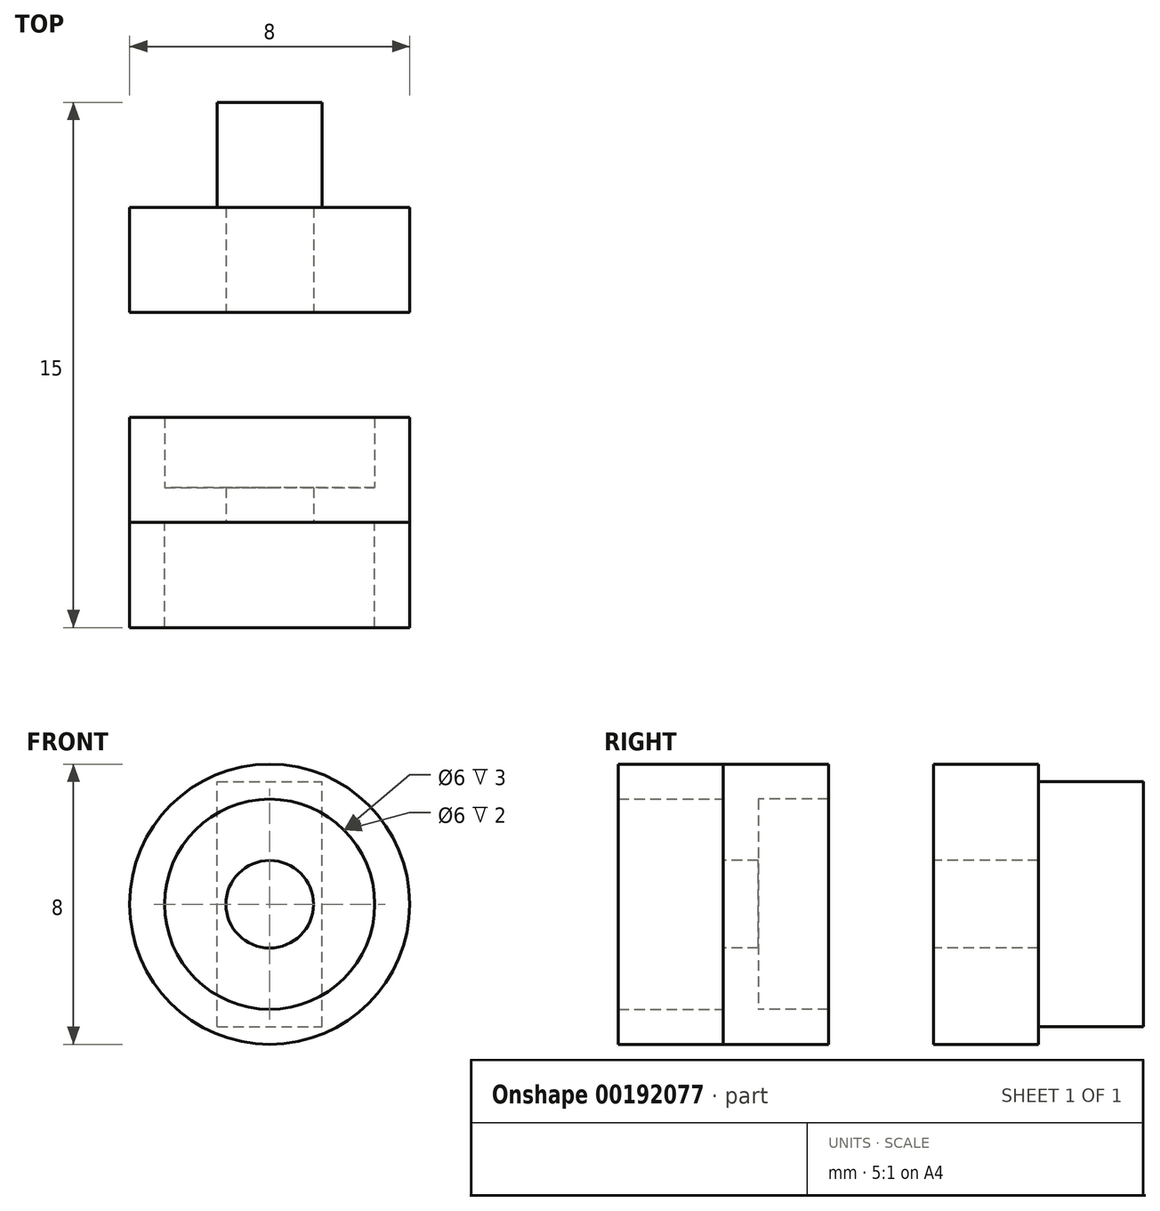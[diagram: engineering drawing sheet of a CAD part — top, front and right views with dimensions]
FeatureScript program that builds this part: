
annotation { "Feature Type Name" : "Feature", "Feature Type Description" : "" }
export const myFeature = defineFeature(function(context is Context, id is Id, definition is map)
    precondition{}
    {
        {
            var Q0;
            Q0=qCreatedBy(makeId("Front.planeOp"),FACE);
            var sketch = newSketch(context, id + "F0", { "sketchPlane" : qUnion([Q0])});
            skCircle(sketch, "E0", {"center": v(0, 0) * mm, "radius": 4 * mm});
            skSolve(sketch);
        }
        {
            var Q0;
            Q0 = qSketchRegion(id + "F0", true);
            extrude(context, id + "F1", {"entities" : qUnion([Q0]), "depth" : 1 * mm});
        }
        {
            var Q0;
            Q0=makeQuery(id+"F1.opExtrude","CAP_FACE",FACE,{"disambiguationData":[OSD([sQuery(id+"F0.wireOp",EDGE,"cq2fFx1E-zUqv-iU8P-xQMs-zw5kZQLWphNt"),sQuery(id+"F0.wireOp",EDGE,"E0")])],"isStart":true});
            var sketch = newSketch(context, id + "F2", { "sketchPlane" : qUnion([Q0])});
            skCircle(sketch, "E1", {"center": v(0, 0) * mm, "radius": 4 * mm});
            skCircle(sketch, "E2", {"center": v(0, 0) * mm, "radius": 3 * mm});
            skSolve(sketch);
        }
        {
            var Q0;
            Q0 = qSketchRegion(id + "F2", true);
            extrude(context, id + "F3", {"entities" : qUnion([Q0]), "operationType" : NewBodyOperationType.ADD, "depth" : 2 * mm});
        }
        {
            var Q0;
            Q0=makeQuery(id+"F1.opExtrude","CAP_FACE",FACE,{"disambiguationData":[OSD([sQuery(id+"F0.wireOp",EDGE,"E0")])],"isStart":false});
            var sketch = newSketch(context, id + "F4", { "sketchPlane" : qUnion([Q0])});
            skCircle(sketch, "E3", {"center": v(0, 0) * mm, "radius": 1.25 * mm});
            skSolve(sketch);
        }
        {
            var Q0;
            Q0 = qSketchRegion(id + "F4", true);
            extrude(context, id + "F5", {"entities" : qUnion([Q0]), "operationType" : NewBodyOperationType.REMOVE, "oppositeDirection" : true, "depth" : 25 * mm});
        }
        {
            var Q0;
            Q0=makeQuery(id+"F1.opExtrude","CAP_FACE",FACE,{"disambiguationData":[OSD([sQuery(id+"F0.wireOp",EDGE,"E0")])],"isStart":false});
            var sketch = newSketch(context, id + "F6", { "sketchPlane" : qUnion([Q0])});
            skCircle(sketch, "E4", {"center": v(0, 0) * mm, "radius": 4 * mm});
            skCircle(sketch, "E5", {"center": v(0, 0) * mm, "radius": 3 * mm});
            skSolve(sketch);
        }
        {
            var Q0;
            Q0 = qSketchRegion(id + "F6", true);
            extrude(context, id + "F7", {"entities" : qUnion([Q0]), "depth" : 3 * mm});
        }
        {
            var Q0;
            Q0=qCreatedBy(makeId("Front.planeOp"),FACE);
            cPlane(context, id + "F8", {"entities" : qUnion([Q0]), "cplaneType" : CPlaneType.OFFSET, "offset" : 5 * mm, "oppositeDirection" : true, "width" : 150 * mm, "height" : 150 * mm});
        }
        {
            var Q0;
            Q0=qCreatedBy(id+"F8.planeOp",FACE);
            var sketch = newSketch(context, id + "F9", { "sketchPlane" : qUnion([Q0])});
            skCircle(sketch, "E6", {"center": v(0, 0) * mm, "radius": 4 * mm});
            skSolve(sketch);
        }
        {
            var Q0;
            Q0 = qSketchRegion(id + "F9", true);
            extrude(context, id + "F10", {"entities" : qUnion([Q0]), "oppositeDirection" : true, "depth" : 3 * mm});
        }
        {
            var Q0;
            Q0=qCreatedBy(id+"F8.planeOp",FACE);
            cPlane(context, id + "F11", {"entities" : qUnion([Q0]), "cplaneType" : CPlaneType.OFFSET, "offset" : 4 * mm, "oppositeDirection" : true, "width" : 150 * mm, "height" : 150 * mm});
        }
        {
            var Q0;
            Q0=qCreatedBy(id+"F8.planeOp",FACE);
            var sketch = newSketch(context, id + "F12", { "sketchPlane" : qUnion([Q0])});
            skCircle(sketch, "E7", {"center": v(0, 0) * mm, "radius": 1.25 * mm});
            skSolve(sketch);
        }
        {
            var Q0;
            Q0 = qSketchRegion(id + "F12", true);
            extrude(context, id + "F13", {"entities" : qUnion([Q0]), "operationType" : NewBodyOperationType.REMOVE, "oppositeDirection" : true, "depth" : 3 * mm});
        }
        {
            var Q0;
            Q0=makeQuery(id+"F10.opExtrude","CAP_FACE",FACE,{"disambiguationData":[OSD([sQuery(id+"F9.wireOp",EDGE,"E6")])],"isStart":false});
            var sketch = newSketch(context, id + "F14", { "sketchPlane" : qUnion([Q0])});
            skLineSegment(sketch, "E8.bottom", {"start": v(1.5, -3.5) * mm, "end": v(-1.5, -3.5) * mm});
            skLineSegment(sketch, "E8.top", {"start": v(1.5, 3.5) * mm, "end": v(-1.5, 3.5) * mm});
            skLineSegment(sketch, "E8.left", {"start": v(1.5, -3.5) * mm, "end": v(1.5, 3.5) * mm});
            skLineSegment(sketch, "E8.right", {"start": v(-1.5, -3.5) * mm, "end": v(-1.5, 3.5) * mm});
            skPoint(sketch, "E8.middle", {"position": v(0, 0) * mm});
            skSolve(sketch);
        }
        {
            var Q0;
            Q0 = qSketchRegion(id + "F14", true);
            extrude(context, id + "F15", {"entities" : qUnion([Q0]), "operationType" : NewBodyOperationType.ADD, "depth" : 3 * mm});
        }
    });
